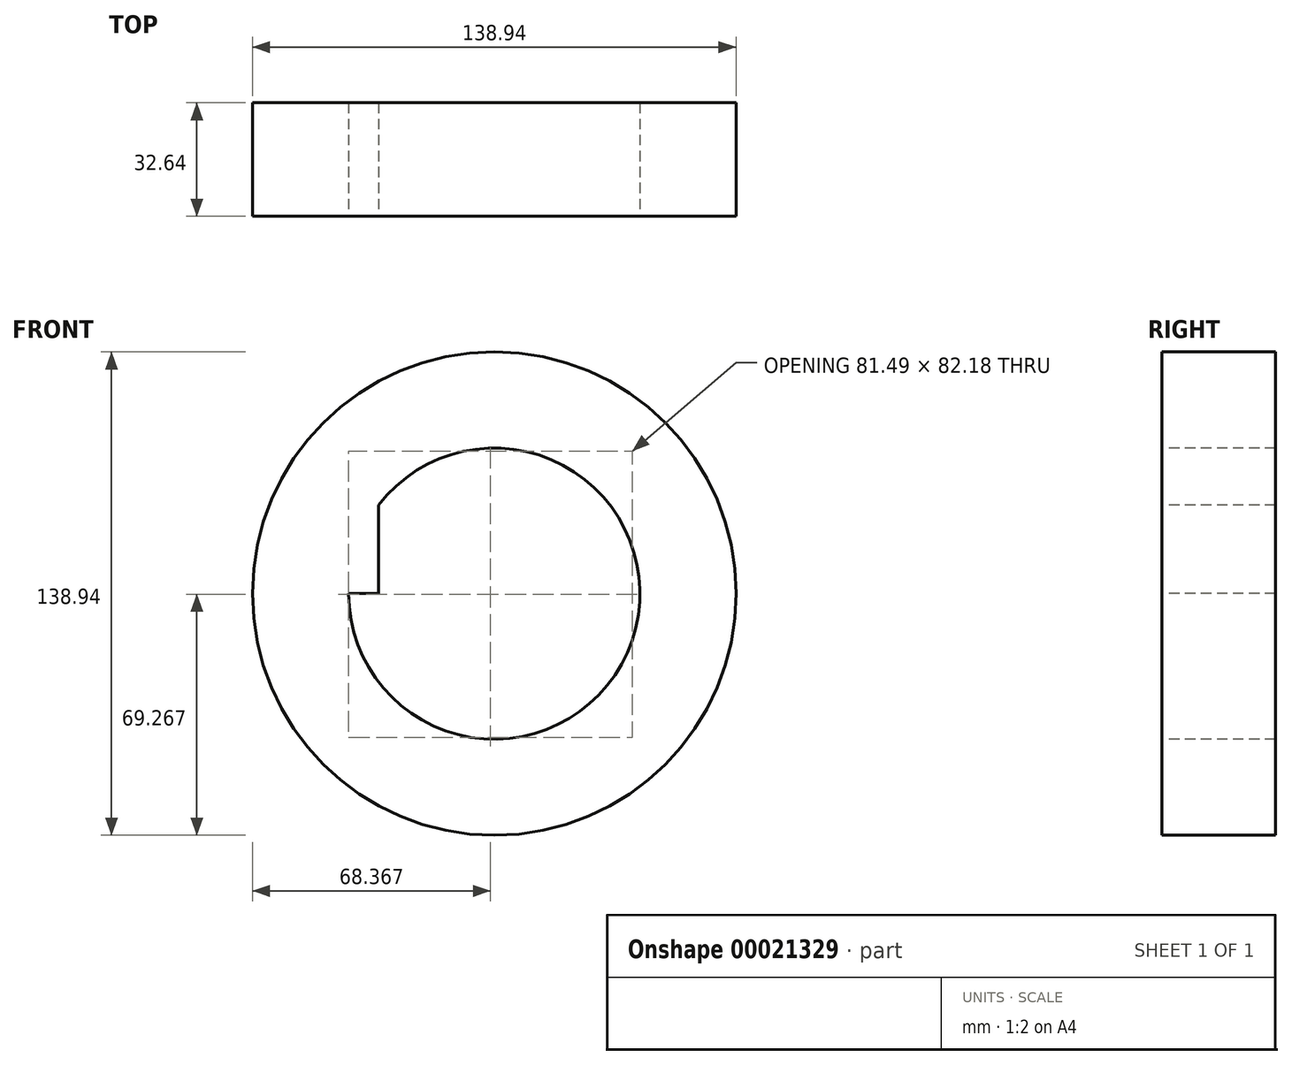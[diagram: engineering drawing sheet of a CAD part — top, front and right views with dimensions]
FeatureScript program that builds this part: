
annotation { "Feature Type Name" : "Feature", "Feature Type Description" : "" }
export const myFeature = defineFeature(function(context is Context, id is Id, definition is map)
    precondition{}
    {
        {
            var Q0;
            Q0=qCreatedBy(makeId("Top.planeOp"),FACE);
            var sketch = newSketch(context, id + "F0", { "sketchPlane" : qUnion([Q0])});
            skLineSegment(sketch, "E0.bottom", {"start": v(-64.66, 19.25) * mm, "end": v(-33.26, 19.25) * mm});
            skLineSegment(sketch, "E0.top", {"start": v(-64.66, -13.4) * mm, "end": v(-33.26, -13.4) * mm});
            skLineSegment(sketch, "E0.left", {"start": v(-64.66, 19.25) * mm, "end": v(-64.66, -13.4) * mm});
            skLineSegment(sketch, "E0.right", {"start": v(-33.26, 19.25) * mm, "end": v(-33.26, -13.4) * mm});
            skLineSegment(sketch, "E1", {"start": v(-127.79, 25.71) * mm, "end": v(-109.31, 58.04) * mm});
            skLineSegment(sketch, "E2", {"start": v(-121.32, 10.62) * mm, "end": v(-146.88, 31.87) * mm});
            skLineSegment(sketch, "E3", {"start": v(-90.22, 45.11) * mm, "end": v(-116.4, -47.57) * mm, "construction": true});
            skLineSegment(sketch, "E4", {"start": v(0, -49.11) * mm, "end": v(0, 48.19) * mm, "construction": true});
            skSolve(sketch);
        }
        {
            var Q0;
            Q0 = qSketchRegion(id + "F0", true);
            extrude(context, id + "F1", {"entities" : qUnion([Q0]), "depth" : 25.4 * mm});
        }
        {
            var Q0;
            Q0=makeQuery(id+"F1.opExtrude","CAP_FACE",FACE,{"disambiguationData":[OSD([sQuery(id+"F0.wireOp",EDGE,"E0.bottom"),sQuery(id+"F0.wireOp",EDGE,"E0.top"),sQuery(id+"F0.wireOp",EDGE,"E0.left"),sQuery(id+"F0.wireOp",EDGE,"E0.right")])],"isStart":false});
            var Q1;
            Q1=sQuery(id+"F0.wireOp",EDGE,"E4");
            revolve(context, id + "F2", {"operationType" : NewBodyOperationType.ADD, "entities" : qUnion([Q0]), "axis" : qUnion([Q1]), "revolveType" : RevolveType.FULL});
        }
    });
